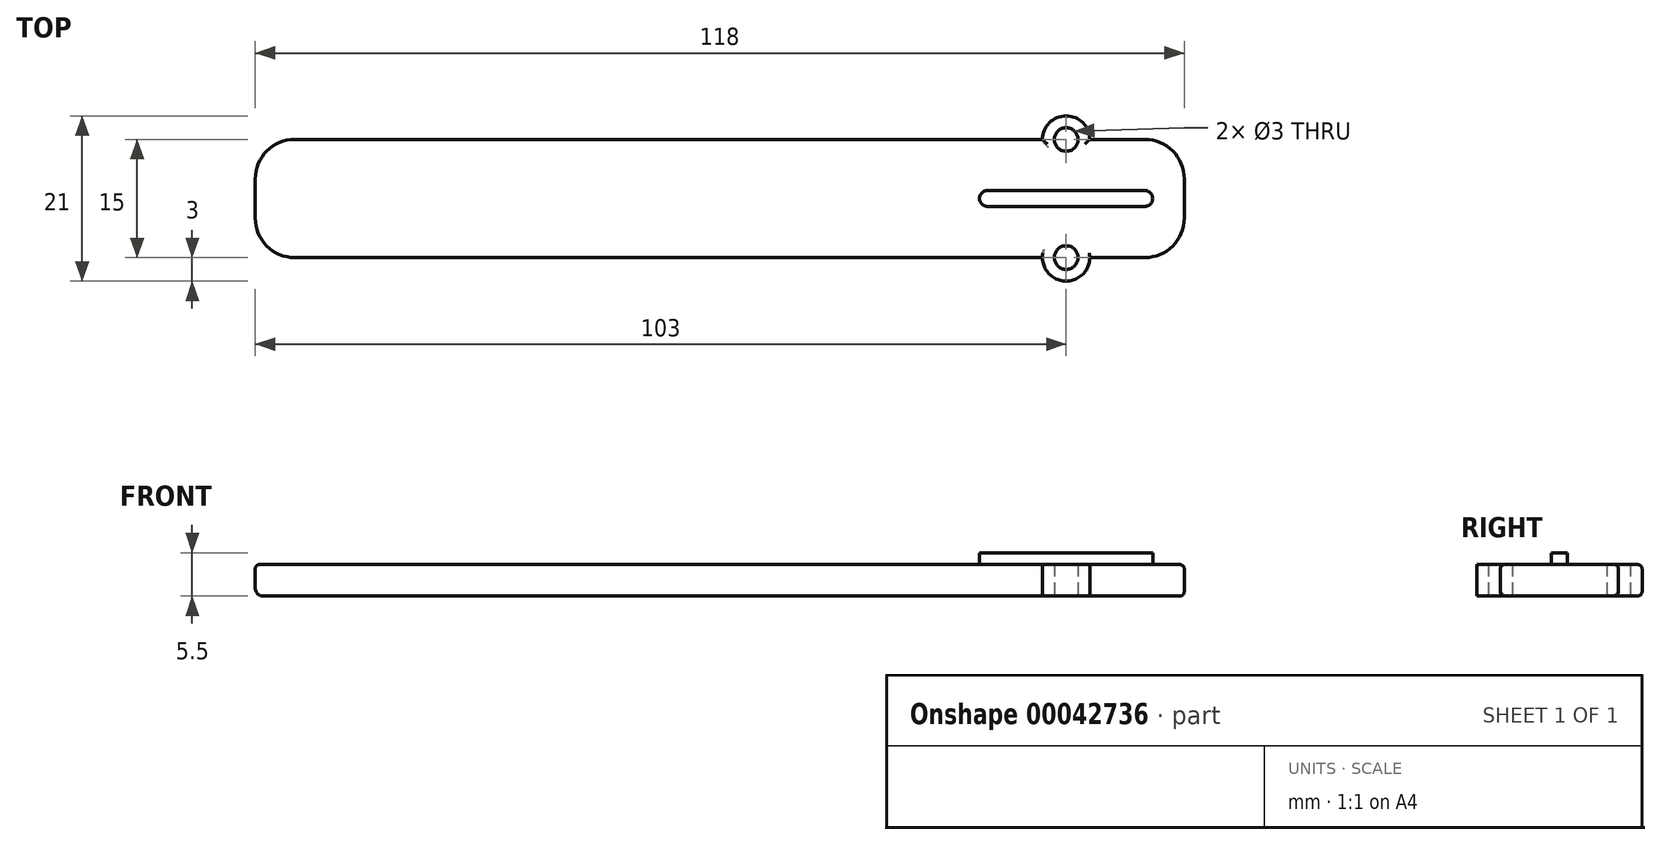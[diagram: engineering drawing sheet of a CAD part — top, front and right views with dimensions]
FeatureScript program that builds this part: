
annotation { "Feature Type Name" : "Feature", "Feature Type Description" : "" }
export const myFeature = defineFeature(function(context is Context, id is Id, definition is map)
    precondition{}
    {
        {
            var Q0;
            Q0=qCreatedBy(makeId("Top.planeOp"),FACE);
            var sketch = newSketch(context, id + "F0", { "sketchPlane" : qUnion([Q0])});
            skLineSegment(sketch, "E0.bottom", {"start": v(0, 0) * mm, "end": v(-95, 0) * mm});
            skLineSegment(sketch, "E0.top", {"start": v(0, 15) * mm, "end": v(-95, 15) * mm});
            skLineSegment(sketch, "E0.right", {"start": v(-100, 5) * mm, "end": v(-100, 10) * mm});
            skPoint(sketch, "E1.visualSharp", {"position": v(-100, 15) * mm});
            skArc(sketch, "E1.filletArc", {"start": v(-95, 15) * mm, "mid": v(-98.54, 13.54) * mm, "end": v(-100, 10) * mm});
            skPoint(sketch, "E2.visualSharp", {"position": v(-100, 0) * mm});
            skArc(sketch, "E2.filletArc", {"start": v(-100, 5) * mm, "mid": v(-98.54, 1.46) * mm, "end": v(-95, 0) * mm});
            skArc(sketch, "E3", {"start": v(6, 15) * mm, "mid": v(3, 18) * mm, "end": v(0, 15) * mm});
            skCircle(sketch, "E4", {"center": v(3, 15) * mm, "radius": 1.5 * mm});
            skLineSegment(sketch, "E5.bottom", {"start": v(6, 15) * mm, "end": v(13, 15) * mm});
            skLineSegment(sketch, "E5.top", {"start": v(6, 0) * mm, "end": v(13, 0) * mm});
            skLineSegment(sketch, "E5.left", {"start": v(6, 15) * mm, "end": v(6, 0) * mm, "construction": true});
            skLineSegment(sketch, "E5.right", {"start": v(18, 10) * mm, "end": v(18, 5) * mm});
            skPoint(sketch, "E6.visualSharp", {"position": v(18, 15) * mm});
            skArc(sketch, "E6.filletArc", {"start": v(18, 10) * mm, "mid": v(16.54, 13.54) * mm, "end": v(13, 15) * mm});
            skPoint(sketch, "E7.visualSharp", {"position": v(18, 0) * mm});
            skArc(sketch, "E7.filletArc", {"start": v(13, 0) * mm, "mid": v(16.54, 1.46) * mm, "end": v(18, 5) * mm});
            skLineSegment(sketch, "E8", {"start": v(18, 7.5) * mm, "end": v(-8.16, 7.5) * mm, "construction": true});
            skCircle(sketch, "E9.MirrorC", {"center": v(3, 0) * mm, "radius": 1.5 * mm});
            skArc(sketch, "E10", {"start": v(0, 0) * mm, "mid": v(3, -3) * mm, "end": v(6, 0) * mm});
            skSolve(sketch);
        }
        {
            var Q0;
            Q0=qSketchRegion(id+"F0",true);
            var Q1;
            Q1=makeQuery(id+"F0.imprint","IMPRINT",FACE,{"disambiguationData":[TD([[makeQuery(id+"F0.imprint","IMPRINT",EDGE,{"derivedFrom":sQuery(id+"F0.wireOp",EDGE,"E0.bottom")}),-1.0]])]});
            extrude(context, id + "F1", {"entities" : qUnion([Q0, Q1]), "depth" : 4 * mm});
        }
        {
            var Q0;
            Q0=makeQuery(id+"F1.opExtrude","CAP_EDGE",EDGE,{"disambiguationData":[OSD([sQuery(id+"F0.wireOp",EDGE,"E0.bottom")])],"isStart":false});
            fillet(context, id + "F2", {"entities" : qUnion([Q0]), "radius" : 0.55 * mm, "tangentPropagation" : true, "allowEdgeOverflow" : false});
        }
        {
            var Q0;
            Q0=makeQuery(id+"F1.opExtrude","CAP_EDGE",EDGE,{"disambiguationData":[OSD([sQuery(id+"F0.wireOp",EDGE,"E0.bottom")])],"isStart":true});
            fillet(context, id + "F3", {"entities" : qUnion([Q0]), "radius" : 1 * mm, "tangentPropagation" : true, "allowEdgeOverflow" : false});
        }
        {
            var Q0;
            Q0=makeQuery(id+"F1.opExtrude","CAP_EDGE",EDGE,{"disambiguationData":[OSD([sQuery(id+"F0.wireOp",EDGE,"d531e0c4-17c8-4529-9161-fa32f8a9aa0b")])],"isStart":false});
            var Q1;
            Q1=makeQuery(id+"F1.opExtrude","CAP_EDGE",EDGE,{"disambiguationData":[OSD([sQuery(id+"F0.wireOp",EDGE,"75a8fdf6-88b0-4338-b9ba-6ad033f037c1")])],"isStart":false});
            var Q2;
            Q2=makeQuery(id+"F1.opExtrude","CAP_EDGE",EDGE,{"disambiguationData":[OSD([sQuery(id+"F0.wireOp",EDGE,"E3")])],"isStart":false});
            var Q3;
            Q3=makeQuery(id+"F1.opExtrude","CAP_EDGE",EDGE,{"disambiguationData":[OSD([sQuery(id+"F0.wireOp",EDGE,"d531e0c4-17c8-4529-9161-fa32f8a9aa0b")])],"isStart":true});
            var Q4;
            Q4=makeQuery(id+"F1.opExtrude","CAP_EDGE",EDGE,{"disambiguationData":[OSD([sQuery(id+"F0.wireOp",EDGE,"75a8fdf6-88b0-4338-b9ba-6ad033f037c1")])],"isStart":true});
            var Q5;
            Q5=makeQuery(id+"F1.opExtrude","CAP_EDGE",EDGE,{"disambiguationData":[OSD([sQuery(id+"F0.wireOp",EDGE,"E3")])],"isStart":true});
            var Q6;
            Q6=makeQuery(id+"F1.opExtrude","CAP_EDGE",EDGE,{"disambiguationData":[OSD([sQuery(id+"F0.wireOp",EDGE,"E5.top")])],"isStart":false});
            var Q7;
            Q7=makeQuery(id+"F1.opExtrude","CAP_EDGE",EDGE,{"disambiguationData":[OSD([sQuery(id+"F0.wireOp",EDGE,"E6.filletArc"),sQuery(id+"F0.wireOp",EDGE,"E7.filletArc")])],"isStart":false});
            var Q8;
            Q8=makeQuery(id+"F1.opExtrude","CAP_EDGE",EDGE,{"disambiguationData":[OSD([sQuery(id+"F0.wireOp",EDGE,"E6.filletArc"),sQuery(id+"F0.wireOp",EDGE,"E7.filletArc")])],"isStart":true});
            var Q9;
            Q9=makeQuery(id+"F1.opExtrude","CAP_EDGE",EDGE,{"disambiguationData":[OSD([sQuery(id+"F0.wireOp",EDGE,"E5.top")])],"isStart":true});
            var Q10;
            Q10=makeQuery(id+"F1.opExtrude","CAP_EDGE",EDGE,{"disambiguationData":[OSD([sQuery(id+"F0.wireOp",EDGE,"E5.bottom")])],"isStart":true});
            var Q11;
            Q11=makeQuery(id+"F1.opExtrude","CAP_EDGE",EDGE,{"disambiguationData":[OSD([sQuery(id+"F0.wireOp",EDGE,"E5.bottom")])],"isStart":false});
            fillet(context, id + "F4", {"entities" : qUnion([Q0, Q1, Q2, Q3, Q4, Q5, Q6, Q7, Q8, Q9, Q10, Q11]), "radius" : 0.55 * mm, "tangentPropagation" : true, "allowEdgeOverflow" : false});
        }
        {
            var Q0;
            Q0=qCreatedBy(makeId("Top.planeOp"),FACE);
            var sketch = newSketch(context, id + "F5", { "sketchPlane" : qUnion([Q0])});
            skLineSegment(sketch, "E11", {"start": v(3, 15) * mm, "end": v(3, 0) * mm, "construction": true});
            skLineSegment(sketch, "E12", {"start": v(-7, 5) * mm, "end": v(3, 5) * mm, "construction": true});
            skPoint(sketch, "E13", {"position": v(-7, 7.5) * mm});
            skArc(sketch, "E14", {"start": v(-7, 8.5) * mm, "mid": v(-8, 7.5) * mm, "end": v(-7, 6.5) * mm});
            skArc(sketch, "E15.MirrorC", {"start": v(13, 8.5) * mm, "mid": v(14, 7.5) * mm, "end": v(13, 6.5) * mm});
            skLineSegment(sketch, "E16.bottom", {"start": v(-7, 6.5) * mm, "end": v(13, 6.5) * mm});
            skLineSegment(sketch, "E16.top", {"start": v(-7, 8.5) * mm, "end": v(13, 8.5) * mm});
            skSolve(sketch);
        }
        {
            var Q0;
            Q0=qSketchRegion(id+"F5",true);
            extrude(context, id + "F6", {"entities" : qUnion([Q0]), "operationType" : NewBodyOperationType.ADD, "depth" : 5.5 * mm});
        }
    });
